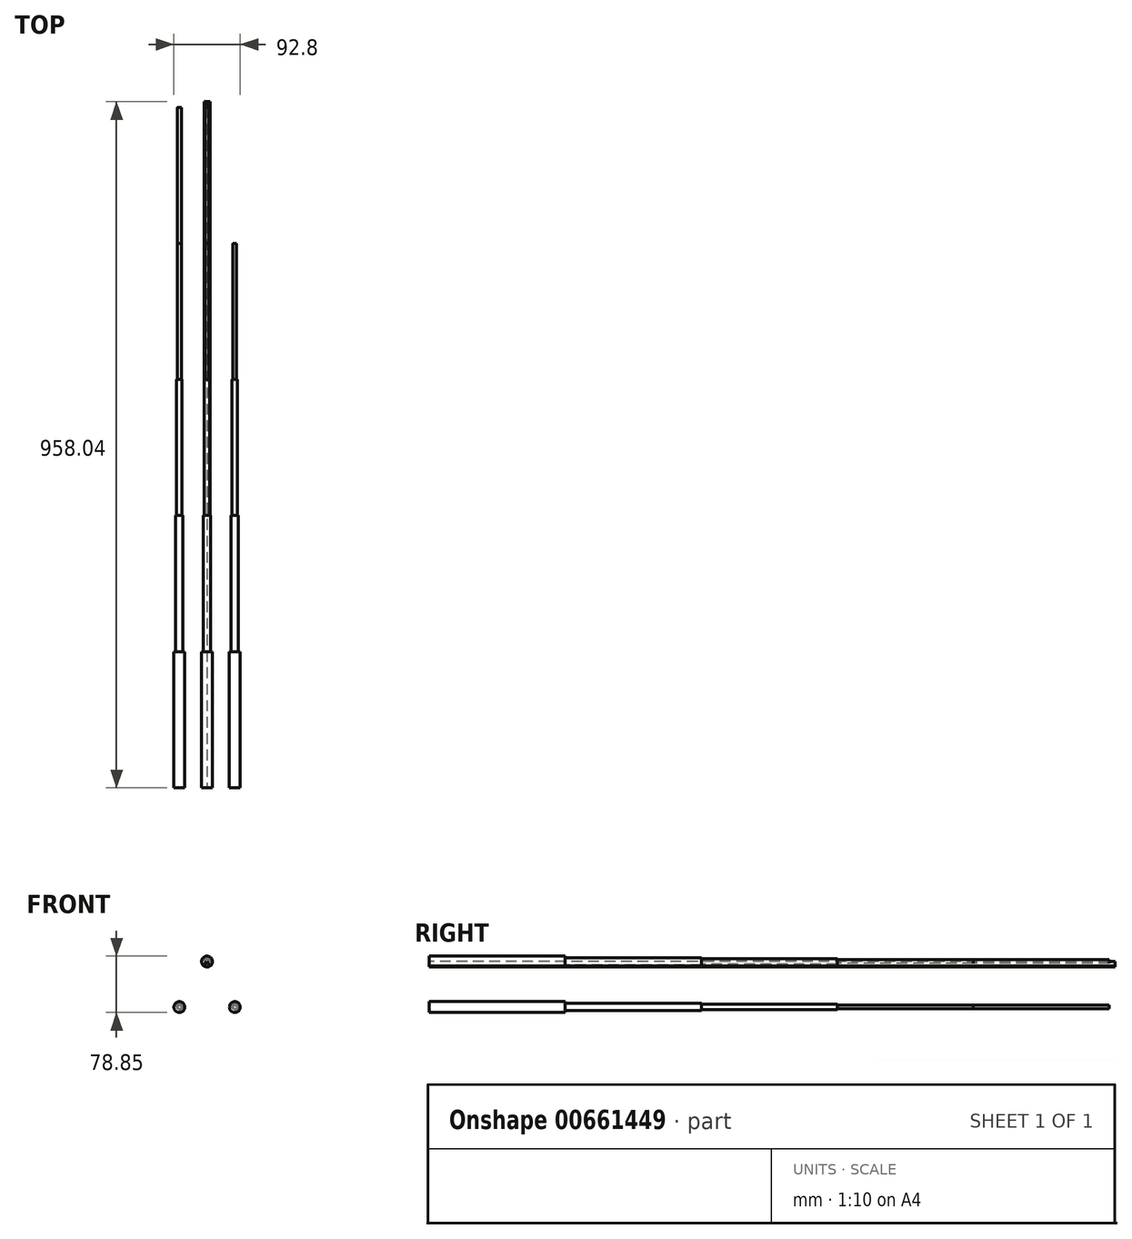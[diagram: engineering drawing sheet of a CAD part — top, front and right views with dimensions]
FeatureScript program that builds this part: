
annotation { "Feature Type Name" : "Feature", "Feature Type Description" : "" }
export const myFeature = defineFeature(function(context is Context, id is Id, definition is map)
    precondition{}
    {
        {
            var Q0;
            Q0=qCreatedBy(makeId("Front.planeOp"),FACE);
            var sketch = newSketch(context, id + "F0", { "sketchPlane" : qUnion([Q0])});
            skCircle(sketch, "E0", {"center": v(38.86, 0) * mm, "radius": 7.62 * mm});
            skCircle(sketch, "E1", {"center": v(0, 63.61) * mm, "radius": 7.62 * mm});
            skCircle(sketch, "E2", {"center": v(-38.7, 0) * mm, "radius": 7.62 * mm});
            skSolve(sketch);
        }
        {
            var Q0;
            Q0=makeQuery(id+"F0.imprint","IMPRINT",FACE,{"disambiguationData":[TD([[makeQuery(id+"F0.imprint","IMPRINT",EDGE,{"derivedFrom":sQuery(id+"F0.wireOp",EDGE,"E1")}),1.0]])]});
            var Q1;
            Q1=makeQuery(id+"F0.imprint","IMPRINT",FACE,{"disambiguationData":[TD([[makeQuery(id+"F0.imprint","IMPRINT",EDGE,{"derivedFrom":sQuery(id+"F0.wireOp",EDGE,"E0")}),1.0]])]});
            var Q2;
            Q2=makeQuery(id+"F0.imprint","IMPRINT",FACE,{"disambiguationData":[TD([[makeQuery(id+"F0.imprint","IMPRINT",EDGE,{"derivedFrom":sQuery(id+"F0.wireOp",EDGE,"E2")}),1.0]])]});
            extrude(context, id + "F1", {"entities" : qUnion([Q0, Q1, Q2]), "depth" : 190 * mm, "offsetDistance" : 25.4 * mm});
        }
        {
            var Q0;
            Q0=makeQuery(id+"F1.opExtrude","CAP_FACE",FACE,{"disambiguationData":[OSD([sQuery(id+"F0.wireOp",EDGE,"E1")])],"isStart":true});
            var sketch = newSketch(context, id + "F2", { "sketchPlane" : qUnion([Q0])});
            skPoint(sketch, "E3", {"position": v(0, 63.61) * mm});
            skSolve(sketch);
        }
        {
            var Q0;
            Q0=makeQuery(id+"F0.imprint","IMPRINT",FACE,{"disambiguationData":[TD([[makeQuery(id+"F0.imprint","IMPRINT",EDGE,{"derivedFrom":sQuery(id+"F0.wireOp",EDGE,"E0")}),1.0]])]});
            var sketch = newSketch(context, id + "F3", { "sketchPlane" : qUnion([Q0])});
            skCircle(sketch, "E4", {"center": v(0, 63.74) * mm, "radius": 5.08 * mm});
            skCircle(sketch, "E5", {"center": v(38.85, 0) * mm, "radius": 5.08 * mm});
            skCircle(sketch, "E6", {"center": v(-38.6, 0) * mm, "radius": 5.08 * mm});
            skSolve(sketch);
        }
        {
            var Q0;
            Q0=makeQuery(id+"F3.imprint","IMPRINT",FACE,{"disambiguationData":[TD([[makeQuery(id+"F3.imprint","IMPRINT",EDGE,{"derivedFrom":sQuery(id+"F3.wireOp",EDGE,"E5")}),1.0]])]});
            var Q1;
            Q1=makeQuery(id+"F3.imprint","IMPRINT",FACE,{"disambiguationData":[TD([[makeQuery(id+"F3.imprint","IMPRINT",EDGE,{"derivedFrom":sQuery(id+"F3.wireOp",EDGE,"E4")}),1.0]])]});
            var Q2;
            Q2=makeQuery(id+"F3.imprint","IMPRINT",FACE,{"disambiguationData":[TD([[makeQuery(id+"F3.imprint","IMPRINT",EDGE,{"derivedFrom":sQuery(id+"F3.wireOp",EDGE,"E6")}),1.0]])]});
            var Q3;
            Q3=makeQuery(id+"F1.opExtrude","CAP_FACE",FACE,{"disambiguationData":[OSD([sQuery(id+"F0.wireOp",EDGE,"E1")])],"isStart":false});
            extrude(context, id + "F4", {"entities" : qUnion([Q0, Q1, Q2, Q3]), "operationType" : NewBodyOperationType.ADD, "oppositeDirection" : true, "depth" : 190 * mm, "offsetDistance" : 25.4 * mm});
        }
        {
            var Q0;
            Q0=makeQuery(id+"F4.opExtrude","CAP_FACE",FACE,{"disambiguationData":[OSD([sQuery(id+"F3.wireOp",EDGE,"E5")])],"isStart":false});
            var sketch = newSketch(context, id + "F5", { "sketchPlane" : qUnion([Q0])});
            skCircle(sketch, "E7", {"center": v(-38.85, 0) * mm, "radius": 3.81 * mm});
            skCircle(sketch, "E8", {"center": v(38.6, 0) * mm, "radius": 3.81 * mm});
            skCircle(sketch, "E9", {"center": v(0, 63.56) * mm, "radius": 3.81 * mm});
            skSolve(sketch);
        }
        {
            var Q0;
            Q0=makeQuery(id+"F5.imprint","IMPRINT",FACE,{"disambiguationData":[TD([[makeQuery(id+"F5.imprint","IMPRINT",EDGE,{"derivedFrom":sQuery(id+"F5.wireOp",EDGE,"E9")}),1.0]])]});
            var Q1;
            Q1=makeQuery(id+"F5.imprint","IMPRINT",FACE,{"disambiguationData":[TD([[makeQuery(id+"F5.imprint","IMPRINT",EDGE,{"derivedFrom":sQuery(id+"F5.wireOp",EDGE,"E8")}),1.0]])]});
            var Q2;
            Q2=makeQuery(id+"F5.imprint","IMPRINT",FACE,{"disambiguationData":[TD([[makeQuery(id+"F5.imprint","IMPRINT",EDGE,{"derivedFrom":sQuery(id+"F5.wireOp",EDGE,"E7")}),1.0]])]});
            extrude(context, id + "F6", {"entities" : qUnion([Q0, Q1, Q2]), "operationType" : NewBodyOperationType.ADD, "depth" : 190 * mm, "offsetDistance" : 25.4 * mm});
        }
        {
            var Q0;
            Q0=makeQuery(id+"F6.opExtrude","CAP_FACE",FACE,{"disambiguationData":[OSD([sQuery(id+"F5.wireOp",EDGE,"E7")])],"isStart":false});
            var sketch = newSketch(context, id + "F7", { "sketchPlane" : qUnion([Q0])});
            skCircle(sketch, "E10", {"center": v(-38.85, 0) * mm, "radius": 2.54 * mm});
            skCircle(sketch, "E11", {"center": v(0, 63.56) * mm, "radius": 2.54 * mm});
            skCircle(sketch, "E12", {"center": v(38.6, 0) * mm, "radius": 2.54 * mm});
            skSolve(sketch);
        }
        {
            var Q0;
            Q0=makeQuery(id+"F7.imprint","IMPRINT",FACE,{"disambiguationData":[TD([[makeQuery(id+"F7.imprint","IMPRINT",EDGE,{"derivedFrom":sQuery(id+"F7.wireOp",EDGE,"E10")}),1.0]])]});
            var Q1;
            Q1=makeQuery(id+"F7.imprint","IMPRINT",FACE,{"disambiguationData":[TD([[makeQuery(id+"F7.imprint","IMPRINT",EDGE,{"derivedFrom":sQuery(id+"F7.wireOp",EDGE,"E12")}),1.0]])]});
            var Q2;
            Q2=makeQuery(id+"F7.imprint","IMPRINT",FACE,{"disambiguationData":[TD([[makeQuery(id+"F7.imprint","IMPRINT",EDGE,{"derivedFrom":sQuery(id+"F7.wireOp",EDGE,"E11")}),1.0]])]});
            extrude(context, id + "F8", {"entities" : qUnion([Q0, Q1, Q2]), "depth" : 190 * mm, "offsetDistance" : 25.4 * mm});
        }
        {
            var Q0;
            Q0=makeQuery(id+"F8.opExtrude","CAP_FACE",FACE,{"disambiguationData":[OSD([sQuery(id+"F7.wireOp",EDGE,"E10")])],"isStart":false});
            var sketch = newSketch(context, id + "F9", { "sketchPlane" : qUnion([Q0])});
            skSolve(sketch);
        }
        {
            var Q0;
            Q0=makeQuery(id+"F8.opExtrude","CAP_FACE",FACE,{"disambiguationData":[OSD([sQuery(id+"F7.wireOp",EDGE,"E11")])],"isStart":false});
            var Q1;
            Q1=makeQuery(id+"F8.opExtrude","CAP_FACE",FACE,{"disambiguationData":[OSD([sQuery(id+"F7.wireOp",EDGE,"E12")])],"isStart":false});
            var Q2;
            Q2=makeQuery(id+"F9.imprint","IMPRINT",FACE,{"disambiguationData":[TD([[makeQuery(id+"F9.imprint","IMPRINT",EDGE,{"derivedFrom":makeQuery(id+"F8.opExtrude","CAP_EDGE",EDGE,{"disambiguationData":[OSD([sQuery(id+"F7.wireOp",EDGE,"E10")])],"isStart":false})}),1.0]])]});
            extrude(context, id + "F10", {"entities" : qUnion([Q0, Q1, Q2]), "depth" : 190 * mm, "offsetDistance" : 25.4 * mm});
        }
        {
            var Q0;
            Q0=makeQuery(id+"F1.opExtrude","CAP_FACE",FACE,{"disambiguationData":[OSD([sQuery(id+"F0.wireOp",EDGE,"E1")])],"isStart":false});
            var sketch = newSketch(context, id + "F11", { "sketchPlane" : qUnion([Q0])});
            skLineSegment(sketch, "E13", {"start": v(-43.47, 0) * mm, "end": v(43.5, 0) * mm});
            skLineSegment(sketch, "E14", {"start": v(-38.72, 0) * mm, "end": v(0, 63.61) * mm});
            skLineSegment(sketch, "E15", {"start": v(0, 63.61) * mm, "end": v(39.1, 0) * mm});
            skLineSegment(sketch, "E16", {"start": v(39.1, 0) * mm, "end": v(-38.72, 0) * mm});
            skSolve(sketch);
        }
        {
            var Q0;
            {var subQ0=sQuery(id+"F11.wireOp",EDGE,"E15");var subQ1=sQuery(id+"F11.wireOp",EDGE,"E14");var subQ2=makeQuery(id+"F11.imprint","INTERSECT",VERTEX,{"derivedFrom":[subQ1,subQ0]});Q0=makeQuery(id+"F11.imprint","IMPRINT",FACE,{"disambiguationData":[TD([[makeQuery(id+"F11.imprint","IMPRINT",EDGE,{"disambiguationData":[TD([[subQ2,1.0]])],"derivedFrom":subQ1}),1.0]])]});}
            extrude(context, id + "F12", {"entities" : qUnion([Q0]), "depth" : 0.13 * mm, "offsetDistance" : 25.4 * mm});
        }
        {
            var Q0;
            {var subQ0=sQuery(id+"F11.wireOp",EDGE,"E15");var subQ1=sQuery(id+"F11.wireOp",EDGE,"E14");var subQ2=makeQuery(id+"F11.imprint","INTERSECT",VERTEX,{"derivedFrom":[subQ1,subQ0]});Q0=makeQuery(id+"F11.imprint","IMPRINT",FACE,{"disambiguationData":[TD([[makeQuery(id+"F11.imprint","IMPRINT",EDGE,{"disambiguationData":[TD([[subQ2,1.0]])],"derivedFrom":subQ1}),-1.0]])]});}
            var Q1;
            {var subQ0=sQuery(id+"F11.wireOp",EDGE,"E16");Q1=makeQuery(id+"F11.imprint","IMPRINT",FACE,{"disambiguationData":[TD([[makeQuery(id+"F11.imprint","IMPRINT",EDGE,{"derivedFrom":subQ0}),-1.0]])]});}
            extrude(context, id + "F13", {"entities" : qUnion([Q0, Q1]), "endBound" : BoundingType.THROUGH_ALL, "oppositeDirection" : true, "depth" : 25.4 * mm, "offsetDistance" : 25.4 * mm});
        }
    });
